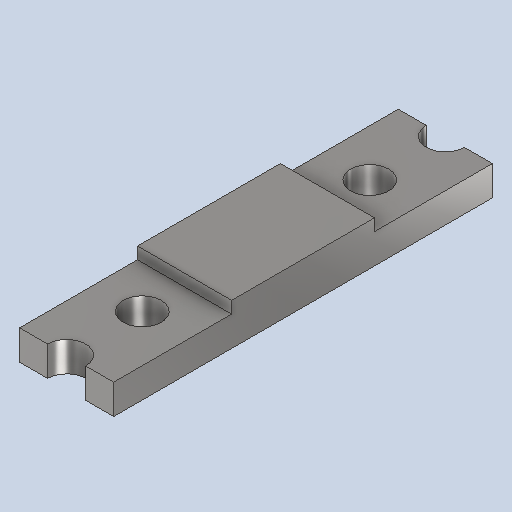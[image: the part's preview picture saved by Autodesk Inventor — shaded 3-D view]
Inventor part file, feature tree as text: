
AUTODESK INVENTOR PART (.ipt)
format: ipt  version: 2024.2 (Build 282272000, 272)  size: 264,704 bytes
history: native  units: mm
features: extrude x2
ambient origin geometry x8: Origin, YZ Plane, XZ Plane, XY Plane, X Axis, Y Axis, Z Axis, Center Point
bodies: Solid1 (feature_tree)
feature tree (2):
  extrude  "Extrusion1"  Depth=31.8mm
  extrude  "Extrusion2"  Depth=7.9mm
